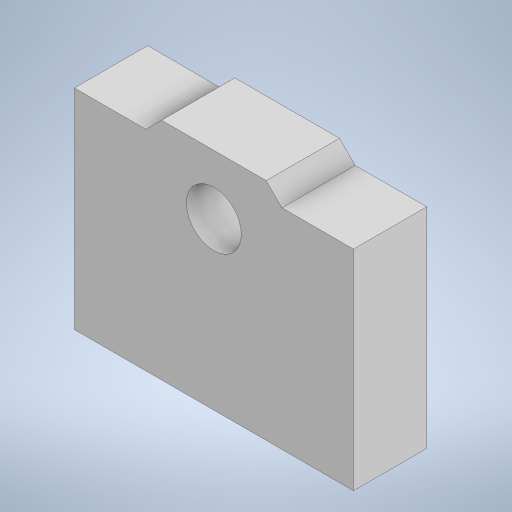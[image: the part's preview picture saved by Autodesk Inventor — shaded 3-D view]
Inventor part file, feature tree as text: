
AUTODESK INVENTOR PART (.ipt)
format: ipt  version: 2024 (Build 280153020, 153B)  size: 314,880 bytes
history: native  units: in
note: dims shown in document units (in); Inventor stores cm internally (conversion verified against a paired STEP export)
features: sketch x9, extrude x8, plane x3, projected_geometry x3, chamfer x1, loft x1
ambient origin geometry x8: Origin, YZ Plane, XZ Plane, XY Plane, X Axis, Y Axis, Z Axis, Center Point
bodies: Solid1 (feature_tree)
feature tree (25):
  extrude  "Extrusion1"  Depth=0.5in
  sketch  "Sketch4"  dims[d2=1.2in d3=0.0in d4=0.95in]
  extrude  "Extrusion2"  Depth=1.2in
  extrude  "Extrusion3"  Depth=0.6in
  chamfer  "Chamfer1"  Distance=1.2in
  extrude  "Extrusion4"  Depth=0.0898in TaperAngle=45.0deg
  plane  "Work Plane1"
  extrude  "Extrusion5"  Depth=0.5in
  sketch  "Sketch7"  dims[d14=0.5in d15=0.5in]
  plane  "Work Plane2"
  loft  "Loft1"
  extrude  "Extrusion6"  [1 undecoded]
  plane  "Work Plane3"
  extrude  "Extrusion7"  Depth=0.0625in
  extrude  "Extrusion8"  TaperAngle=0.0deg  [1 undecoded]
  sketch  "Sketch3"  dims[d0=1.6in d1=0.5in]
  sketch  "Sketch5"  dims[d5=0.315in d6=0.6in d7=1.2in d8=0.0in]
  sketch  "Sketch6"  dims[d9=0.875in d10=0.0in d11=0.0898in d12=0.125in d13=45.0deg]
  projected_geometry  "Projected Loop1"
  sketch  "Sketch8"  dims[d16=0.1299in d17=0.1299in]
  sketch  "Sketch9"  dims[d18=0.7874in d19=0.0in d20=-0.08in]
  projected_geometry  "Projected Loop2"
  sketch  "Sketch10"  dims[d21=0.7874in d22=0.0in d24=0.0625in]
  projected_geometry  "Projected Loop3"
  sketch  "Sketch11"  dims[d25=0.4331in d26=0.0in d27=90.0deg d28=0.0in d29=90.0deg d30=5.0876in d31=0.0in d32=-0.4in d34=0.1112in d35=0.1112in d36=0.1083in d37=0.0in d38=0.3917in d39=0.0in]
note: 2 required parameter values undecoded (feature->parameter linkage not recoverable at this tier; creation-order binding heuristic only, values carry confidence <= 0.55)
